# Revit family: DAL_A3-A108
name_source: partatom
category: Windows
revit_build: Autodesk Revit 2016 (Build: 20150220_1215(x64)
units: mm (PartAtom-declared; Revit-internal decimal feet)

## family parameters
Always vertical = Yes
Cut with Voids When Loaded = No
Host = Wall
Room Calculation Point = No
Shared = No

## types (1)
- 2970w x 2465h
    Array = 3
    Arrays = 3.3
    Bumper Rail Height = 850 mm  [stored 2.78871 ft]
    Construction Type = A108
    Door Head Height = 2465 mm  [stored 8.08727 ft]
    Frame Finish = Metal Aluminium
    Glass Finish = Glass 2
    Head Height = 2465 mm  [stored 8.08727 ft]
    Height = 2465 mm  [stored 8.08727 ft]
    Mullions = 2
    No Of Mullions = 2
    Panel Size = 900 mm  [stored 2.95276 ft]
    Panel Width = 979 mm
    PanelDivides = 3
    Wall Closure = By host
    Width = 2970 mm  [stored 9.74409 ft]

note: [stored X ft] marks values corroborated as IEEE doubles in the binary element streams (Revit-internal decimal feet)

## geometry (parser evidence)
native form markers: Sweep x8
no freeform markers — native parametric forms only
